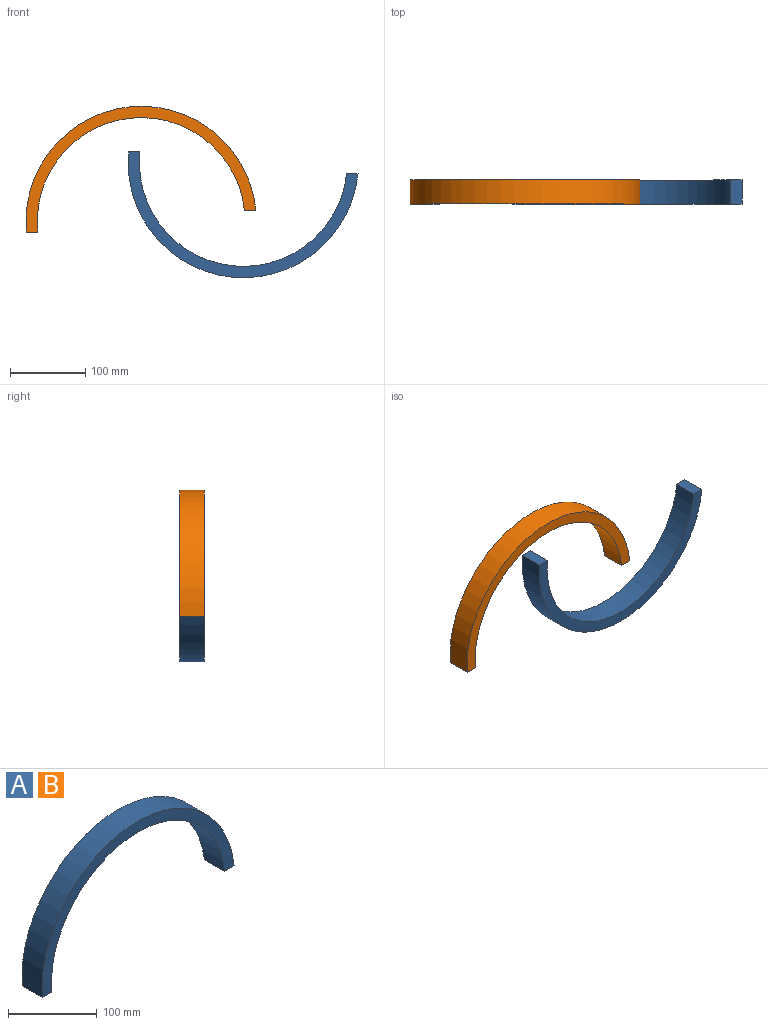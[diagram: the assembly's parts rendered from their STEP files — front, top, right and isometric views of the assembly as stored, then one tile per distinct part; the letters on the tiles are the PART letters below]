
ASSEMBLY  parts=2 mates=1
PART A: 6 faces, bbox 305.3x32x167 mm
  f0: plane 32x15.08mm, normal (0,0,-1), area 482.6mm2, adj f1,f3,f4,f5
  f1: cylinder r=153mm len=305.26mm, axis (0,1,0), area 15349.1mm2, adj f0,f2,f4,f5
  f2: plane 32x15.07mm, normal (0,0,-1), area 482.2mm2, adj f1,f3,f4,f5
  f3: cylinder r=138mm len=275.18mm, axis (0,1,0), area 13841.1mm2, adj f0,f2,f4,f5
  f4: plane 305.26x167mm, normal (0,-1,0), area 6841.5mm2, adj f0,f1,f2,f3
  f5: plane 305.26x167mm, normal (0,1,0), area 6841.5mm2, adj f0,f1,f2,f3
PART B: same geometry as A
PLACE A rot(axis=(1,0,0),180deg) t=(113.02,-38.14,88.77)mm
PLACE B t=(-22.55,-6.14,10.32)mm fixed
MATE planar A.f5 <-> B.f4  axis (0,-1,0) through (-31.8,-38.14,102.77)mm
